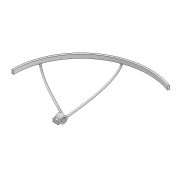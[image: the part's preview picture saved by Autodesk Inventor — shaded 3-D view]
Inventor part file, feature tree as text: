
AUTODESK INVENTOR PART (.ipt)
format: ipt  version: 2022 (Build 260153000, 153)  size: 589,312 bytes
history: native  units: mm
features: sketch x13, plane x7, extrude x6, projected_geometry x5, loft x4
ambient origin geometry x8: Origin, YZ Plane, XZ Plane, XY Plane, X Axis, Y Axis, Z Axis, Center Point
bodies: Solid1 (feature_tree)
feature tree (35):
  extrude  "Extrusion1"  Depth=5.0mm
  plane  "Work Plane1"
  sketch  "Sketch11"  dims[d2=10.0mm d3=0.0mm d4=38.724mm]
  sketch  "Sketch12"  dims[d23=5.0mm d24=30.0mm]
  plane  "Work Plane6"
  sketch  "Sketch13"  dims[d25=6.0mm d33=12.217305mm]
  sketch  "Sketch14"  dims[d35=3.490659mm d42=5.0mm]
  plane  "Work Plane7"
  plane  "Work Plane8"
  loft  "Loft4"
  plane  "Work Plane9"
  loft  "Loft5"
  plane  "Work Plane10"
  sketch  "Sketch20"  dims[d61=0.0mm d62=90.0deg d63=5.0mm]
  extrude  "Extrusion2"  Depth=12.217305mm
  extrude  "Extrusion3"  Depth=5.0mm
  sketch  "Sketch21"  dims[d64=50.0mm d65=-47.0mm]
  extrude  "Extrusion4"  TaperAngle=0.0deg  [1 undecoded]
  extrude  "Extrusion5"  Depth=6.0mm
  extrude  "Extrusion6"  TaperAngle=0.0deg  [1 undecoded]
  plane  "Work Plane11"
  sketch  "Sketch28"  dims[d68=15.0mm d69=0.0mm d70=15.0mm d71=0.0mm d72=1.5mm d73=6.0mm d74=15.0mm d75=0.0mm d76=3.0mm d77=3.0mm d78=15.0mm d79=0.0mm d80=2.2mm d81=2.2mm d82=3.0mm d83=4.0mm d84=4.0mm d85=3.0mm d86=15.0mm d87=0.0mm d89=3.0mm d98=9.0mm d99=9.0mm d110=3.490659mm d111=3.490659mm d113=9.0mm d114=9.0mm d115=0.0mm d116=90.0deg d117=0.0mm d118=90.0deg d119=0.0mm d120=90.0deg d121=0.0mm d122=90.0deg]
  sketch  "Sketch27"  dims[d67=19.0mm]
  loft  "Loft10"
  loft  "Loft11"
  sketch  "Sketch1"  dims[d0=371.0mm d1=5.0mm]
  sketch  "Sketch17"  dims[d50=0.0mm d51=90.0deg d52=0.0mm d53=90.0deg]
  sketch  "Sketch18"  dims[d54=0.0mm d55=90.0deg d56=6.0mm]
  sketch  "Sketch19"  dims[d57=0.0mm d58=90.0deg d59=0.0mm d60=90.0deg]
  projected_geometry  "Projected Loop3"
  sketch  "Sketch22"  dims[d66=12.1mm]
  projected_geometry  "Projected Loop10"
  projected_geometry  "Projected Loop11"
  projected_geometry  "Projected Loop12"
  projected_geometry  "Project Cut Edges3"
note: 2 required parameter values undecoded (feature->parameter linkage not recoverable at this tier; creation-order binding heuristic only, values carry confidence <= 0.55)
